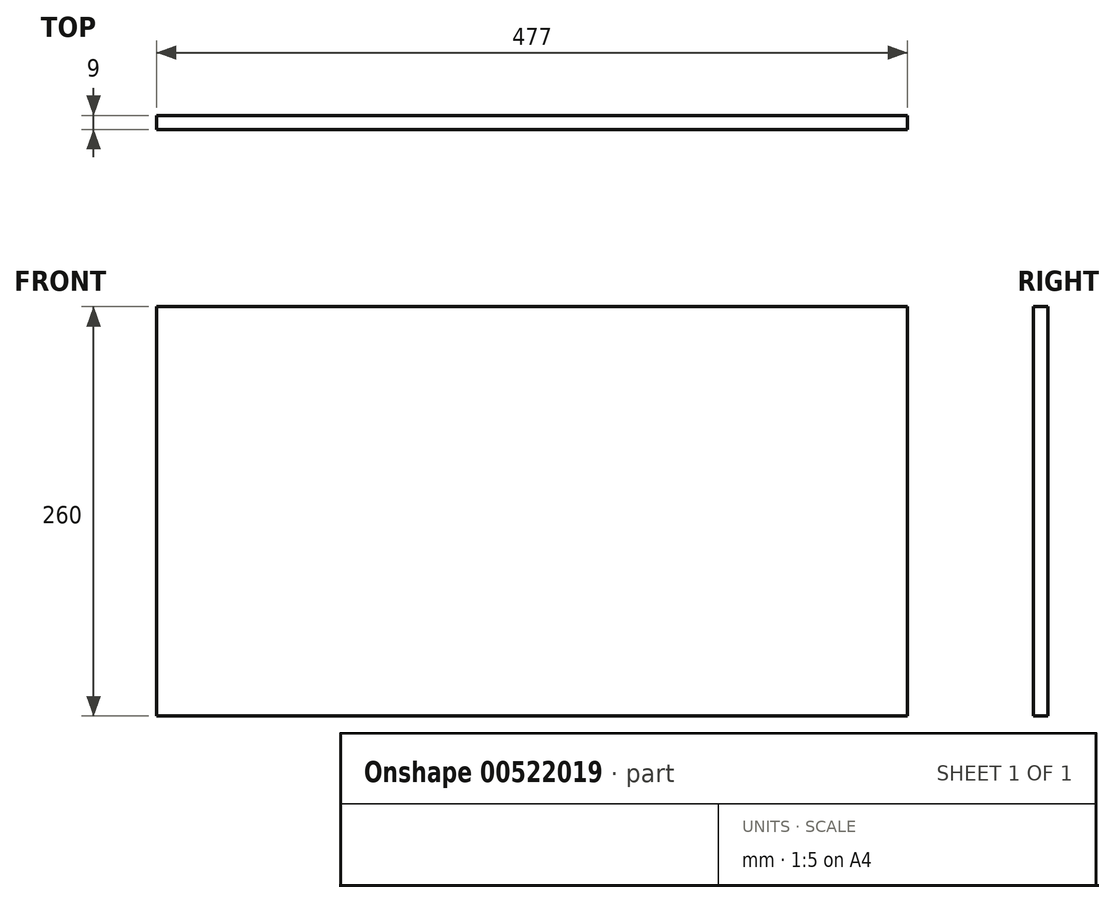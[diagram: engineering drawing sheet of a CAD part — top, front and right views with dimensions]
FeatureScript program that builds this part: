
annotation { "Feature Type Name" : "Feature", "Feature Type Description" : "" }
export const myFeature = defineFeature(function(context is Context, id is Id, definition is map)
    precondition{}
    {
        {
            var Q0;
            Q0=qCreatedBy(makeId("Front.planeOp"),FACE);
            var sketch = newSketch(context, id + "F0", { "sketchPlane" : qUnion([Q0])});
            skLineSegment(sketch, "E0.bottom", {"start": v(0, 0) * mm, "end": v(477, 0) * mm});
            skLineSegment(sketch, "E0.top", {"start": v(0, 260) * mm, "end": v(477, 260) * mm});
            skLineSegment(sketch, "E0.left", {"start": v(0, 0) * mm, "end": v(0, 260) * mm});
            skLineSegment(sketch, "E0.right", {"start": v(477, 0) * mm, "end": v(477, 260) * mm});
            skSolve(sketch);
        }
        {
            var Q0;
            Q0=makeQuery(id+"F0.imprint","IMPRINT",FACE,{"disambiguationData":[TD([[makeQuery(id+"F0.imprint","IMPRINT",EDGE,{"derivedFrom":sQuery(id+"F0.wireOp",EDGE,"E0.bottom")}),1.0]])]});
            extrude(context, id + "F1", {"entities" : qUnion([Q0]), "depth" : 9 * mm, "offsetDistance" : 25 * mm});
        }
    });
